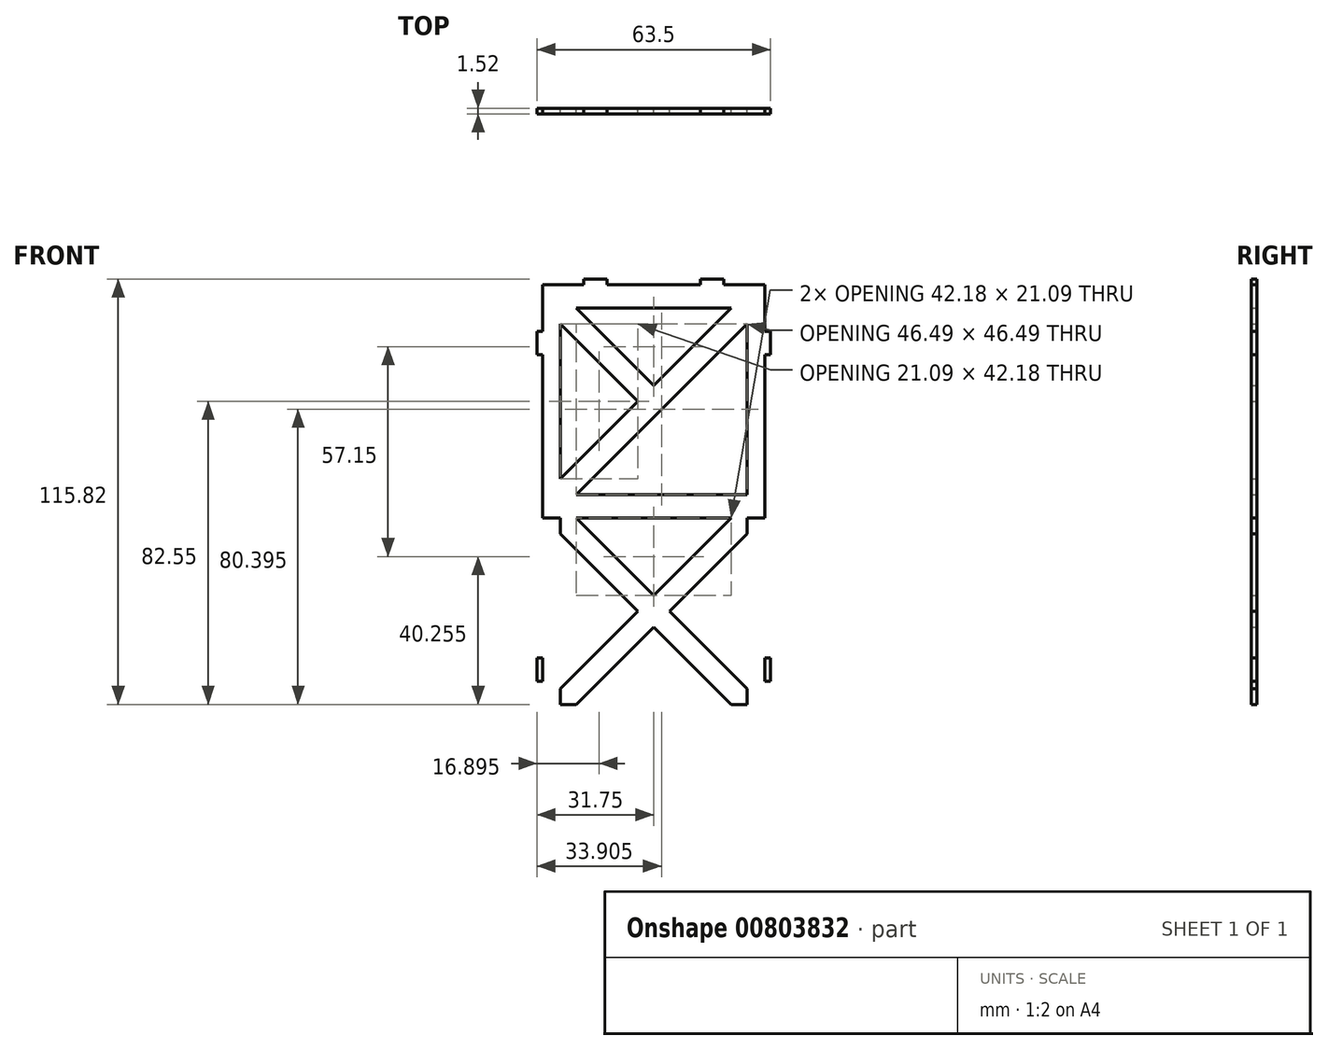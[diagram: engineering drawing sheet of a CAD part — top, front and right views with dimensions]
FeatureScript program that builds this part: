
annotation { "Feature Type Name" : "Feature", "Feature Type Description" : "" }
export const myFeature = defineFeature(function(context is Context, id is Id, definition is map)
    precondition{}
    {
        {
            var Q0;
            Q0=qCreatedBy(makeId("Front.planeOp"),FACE);
            var sketch = newSketch(context, id + "F0", { "sketchPlane" : qUnion([Q0])});
            skLineSegment(sketch, "E0.bottom", {"start": v(31.75, 31.75) * mm, "end": v(-31.75, 31.75) * mm});
            skLineSegment(sketch, "E0.top", {"start": v(31.75, -31.75) * mm, "end": v(-31.75, -31.75) * mm});
            skLineSegment(sketch, "E0.left", {"start": v(31.75, 31.75) * mm, "end": v(31.75, -31.75) * mm});
            skLineSegment(sketch, "E0.right", {"start": v(-31.75, 31.75) * mm, "end": v(-31.75, -31.75) * mm});
            skPoint(sketch, "E0.middle", {"position": v(0, 0) * mm});
            skLineSegment(sketch, "E1.bottom", {"start": v(-19.05, -31.75) * mm, "end": v(-12.7, -31.75) * mm});
            skLineSegment(sketch, "E1.top", {"start": v(-19.05, -33.27) * mm, "end": v(-12.7, -33.27) * mm});
            skLineSegment(sketch, "E1.left", {"start": v(-19.05, -31.75) * mm, "end": v(-19.05, -33.27) * mm});
            skLineSegment(sketch, "E1.right", {"start": v(-12.7, -31.75) * mm, "end": v(-12.7, -33.27) * mm});
            skPoint(sketch, "E2", {"position": v(-15.88, -31.75) * mm});
            skLineSegment(sketch, "E3.MirrorCS", {"start": v(19.05, -31.75) * mm, "end": v(12.7, -31.75) * mm});
            skPoint(sketch, "E4.MirrorP", {"position": v(15.88, -31.75) * mm});
            skLineSegment(sketch, "E5.MirrorCS", {"start": v(19.05, -33.27) * mm, "end": v(12.7, -33.27) * mm});
            skLineSegment(sketch, "E6.MirrorCS", {"start": v(12.7, -31.75) * mm, "end": v(12.7, -33.27) * mm});
            skLineSegment(sketch, "E7.MirrorCS", {"start": v(19.05, -31.75) * mm, "end": v(19.05, -33.27) * mm});
            skLineSegment(sketch, "E8.bottom", {"start": v(-31.75, -19.05) * mm, "end": v(-30.23, -19.05) * mm});
            skLineSegment(sketch, "E8.top", {"start": v(-31.75, -12.7) * mm, "end": v(-30.23, -12.7) * mm});
            skLineSegment(sketch, "E8.left", {"start": v(-31.75, -19.05) * mm, "end": v(-31.75, -12.7) * mm});
            skLineSegment(sketch, "E8.right", {"start": v(-30.23, -19.05) * mm, "end": v(-30.23, -12.7) * mm});
            skPoint(sketch, "E9", {"position": v(-31.75, -15.88) * mm});
            skLineSegment(sketch, "E10.MirrorCS", {"start": v(-31.75, 19.05) * mm, "end": v(-30.23, 19.05) * mm});
            skPoint(sketch, "E11.MirrorP", {"position": v(-31.75, 15.88) * mm});
            skLineSegment(sketch, "E12.MirrorCS", {"start": v(-31.75, 12.7) * mm, "end": v(-30.23, 12.7) * mm});
            skLineSegment(sketch, "E13.MirrorCS", {"start": v(-31.75, 19.05) * mm, "end": v(-31.75, 12.7) * mm});
            skLineSegment(sketch, "E14.MirrorCS", {"start": v(-30.23, 19.05) * mm, "end": v(-30.23, 12.7) * mm});
            skLineSegment(sketch, "E15.MirrorCS", {"start": v(31.75, 19.05) * mm, "end": v(30.23, 19.05) * mm});
            skLineSegment(sketch, "E16.MirrorCS", {"start": v(31.75, -19.05) * mm, "end": v(30.23, -19.05) * mm});
            skLineSegment(sketch, "E17.MirrorCS", {"start": v(31.75, -12.7) * mm, "end": v(30.23, -12.7) * mm});
            skLineSegment(sketch, "E18.MirrorCS", {"start": v(31.75, 12.7) * mm, "end": v(30.23, 12.7) * mm});
            skLineSegment(sketch, "E19.MirrorCS", {"start": v(30.23, 19.05) * mm, "end": v(30.23, 12.7) * mm});
            skLineSegment(sketch, "E20.MirrorCS", {"start": v(30.23, -19.05) * mm, "end": v(30.23, -12.7) * mm});
            skLineSegment(sketch, "E21.MirrorCS", {"start": v(31.75, 19.05) * mm, "end": v(31.75, 12.7) * mm});
            skLineSegment(sketch, "E22.MirrorCS", {"start": v(31.75, -19.05) * mm, "end": v(31.75, -12.7) * mm});
            skPoint(sketch, "E23.MirrorP", {"position": v(31.75, 15.88) * mm});
            skPoint(sketch, "E24.MirrorP", {"position": v(31.75, -15.88) * mm});
            skLineSegment(sketch, "E25.0", {"start": v(-30.23, 31.75) * mm, "end": v(-30.23, -31.75) * mm});
            skLineSegment(sketch, "E26.MirrorCS", {"start": v(30.23, 31.75) * mm, "end": v(30.23, -31.75) * mm});
            skLineSegment(sketch, "E27.bottom", {"start": v(25.4, 25.4) * mm, "end": v(-25.4, 25.4) * mm});
            skLineSegment(sketch, "E27.top", {"start": v(25.4, -25.4) * mm, "end": v(-25.4, -25.4) * mm});
            skLineSegment(sketch, "E27.left", {"start": v(25.4, 25.4) * mm, "end": v(25.4, -25.4) * mm});
            skLineSegment(sketch, "E27.right", {"start": v(-25.4, 25.4) * mm, "end": v(-25.4, -25.4) * mm});
            skLineSegment(sketch, "E28", {"start": v(-25.4, -25.4) * mm, "end": v(25.4, 25.4) * mm, "construction": true});
            skLineSegment(sketch, "E29", {"start": v(-25.4, 25.4) * mm, "end": v(25.4, -25.4) * mm, "construction": true});
            skLineSegment(sketch, "E30.0", {"start": v(-27.56, 23.24) * mm, "end": v(23.24, -27.56) * mm});
            skLineSegment(sketch, "E31.0", {"start": v(-23.24, 27.56) * mm, "end": v(27.56, -23.24) * mm});
            skLineSegment(sketch, "E32.0", {"start": v(-23.24, -27.56) * mm, "end": v(27.56, 23.24) * mm});
            skLineSegment(sketch, "E33.0", {"start": v(-27.56, -23.24) * mm, "end": v(23.24, 27.56) * mm});
            skLineSegment(sketch, "E34.MirrorCS", {"start": v(-12.7, 31.75) * mm, "end": v(-12.7, 33.27) * mm});
            skLineSegment(sketch, "E35.MirrorCS", {"start": v(19.05, 31.75) * mm, "end": v(19.05, 33.27) * mm});
            skLineSegment(sketch, "E36.MirrorCS", {"start": v(12.7, 31.75) * mm, "end": v(12.7, 33.27) * mm});
            skLineSegment(sketch, "E37.MirrorCS", {"start": v(-19.05, 31.75) * mm, "end": v(-19.05, 33.27) * mm});
            skPoint(sketch, "E38.MirrorP", {"position": v(-15.88, 31.75) * mm});
            skLineSegment(sketch, "E39.MirrorCS", {"start": v(19.05, 31.75) * mm, "end": v(12.7, 31.75) * mm});
            skLineSegment(sketch, "E40.MirrorCS", {"start": v(19.05, 33.27) * mm, "end": v(12.7, 33.27) * mm});
            skPoint(sketch, "E41.MirrorP", {"position": v(15.88, 31.75) * mm});
            skLineSegment(sketch, "E42.MirrorCS", {"start": v(-19.05, 33.27) * mm, "end": v(-12.7, 33.27) * mm});
            skLineSegment(sketch, "E43.MirrorCS", {"start": v(-19.05, 31.75) * mm, "end": v(-12.7, 31.75) * mm});
            skLineSegment(sketch, "E44.MirrorCS", {"start": v(19.05, 31.75) * mm, "end": v(19.05, 30.23) * mm});
            skLineSegment(sketch, "E45.MirrorCS", {"start": v(-12.7, 31.75) * mm, "end": v(-12.7, 30.23) * mm});
            skLineSegment(sketch, "E46.MirrorCS", {"start": v(-19.05, 31.75) * mm, "end": v(-19.05, 30.23) * mm});
            skLineSegment(sketch, "E47.MirrorCS", {"start": v(12.7, 31.75) * mm, "end": v(12.7, 30.23) * mm});
            skLineSegment(sketch, "E48.MirrorCS", {"start": v(-19.05, 30.23) * mm, "end": v(-12.7, 30.23) * mm});
            skLineSegment(sketch, "E49.MirrorCS", {"start": v(19.05, 30.23) * mm, "end": v(12.7, 30.23) * mm});
            skLineSegment(sketch, "E50", {"start": v(0, 25.4) * mm, "end": v(0, 31.75) * mm});
            skLineSegment(sketch, "E51", {"start": v(0, 28.58) * mm, "end": v(30.23, 28.58) * mm, "construction": true});
            skLineSegment(sketch, "E52.MirrorCS", {"start": v(-19.05, 25.4) * mm, "end": v(-19.05, 26.92) * mm});
            skLineSegment(sketch, "E53.MirrorCS", {"start": v(19.05, 25.4) * mm, "end": v(19.05, 23.88) * mm});
            skLineSegment(sketch, "E54.MirrorCS", {"start": v(-12.7, 25.4) * mm, "end": v(-12.7, 26.92) * mm});
            skLineSegment(sketch, "E55.MirrorCS", {"start": v(19.05, 25.4) * mm, "end": v(19.05, 26.92) * mm});
            skLineSegment(sketch, "E56.MirrorCS", {"start": v(12.7, 25.4) * mm, "end": v(12.7, 26.92) * mm});
            skLineSegment(sketch, "E57.MirrorCS", {"start": v(-19.05, 25.4) * mm, "end": v(-19.05, 23.88) * mm});
            skLineSegment(sketch, "E58.MirrorCS", {"start": v(12.7, 25.4) * mm, "end": v(12.7, 23.88) * mm});
            skLineSegment(sketch, "E59.MirrorCS", {"start": v(-12.7, 25.4) * mm, "end": v(-12.7, 23.88) * mm});
            skLineSegment(sketch, "E60.MirrorCS", {"start": v(19.05, 25.4) * mm, "end": v(12.7, 25.4) * mm});
            skLineSegment(sketch, "E61.MirrorCS", {"start": v(-19.05, 25.4) * mm, "end": v(-12.7, 25.4) * mm});
            skLineSegment(sketch, "E62.MirrorCS", {"start": v(-31.75, 76.2) * mm, "end": v(-30.23, 76.2) * mm});
            skLineSegment(sketch, "E63.MirrorCS", {"start": v(-19.05, 23.88) * mm, "end": v(-12.7, 23.88) * mm});
            skLineSegment(sketch, "E64.MirrorCS", {"start": v(-31.75, 38.1) * mm, "end": v(-30.23, 38.1) * mm});
            skLineSegment(sketch, "E65.MirrorCS", {"start": v(-19.05, 26.92) * mm, "end": v(-12.7, 26.92) * mm});
            skLineSegment(sketch, "E66.MirrorCS", {"start": v(31.75, 44.45) * mm, "end": v(30.23, 44.45) * mm});
            skLineSegment(sketch, "E67.MirrorCS", {"start": v(31.75, 76.2) * mm, "end": v(30.23, 76.2) * mm});
            skLineSegment(sketch, "E68.MirrorCS", {"start": v(19.05, 26.92) * mm, "end": v(12.7, 26.92) * mm});
            skLineSegment(sketch, "E69.MirrorCS", {"start": v(31.75, 69.85) * mm, "end": v(30.23, 69.85) * mm});
            skLineSegment(sketch, "E70.MirrorCS", {"start": v(-31.75, 69.85) * mm, "end": v(-30.23, 69.85) * mm});
            skLineSegment(sketch, "E71.MirrorCS", {"start": v(19.05, 23.88) * mm, "end": v(12.7, 23.88) * mm});
            skLineSegment(sketch, "E72.MirrorCS", {"start": v(-31.75, 44.45) * mm, "end": v(-30.23, 44.45) * mm});
            skLineSegment(sketch, "E73.MirrorCS", {"start": v(19.05, 88.9) * mm, "end": v(19.05, 90.42) * mm});
            skPoint(sketch, "E74.MirrorP", {"position": v(0, 57.15) * mm});
            skLineSegment(sketch, "E75.MirrorCS", {"start": v(12.7, 88.9) * mm, "end": v(12.7, 90.42) * mm});
            skLineSegment(sketch, "E76.MirrorCS", {"start": v(-12.7, 88.9) * mm, "end": v(-12.7, 90.42) * mm});
            skLineSegment(sketch, "E77.MirrorCS", {"start": v(31.75, 38.1) * mm, "end": v(30.23, 38.1) * mm});
            skLineSegment(sketch, "E78.MirrorCS", {"start": v(-19.05, 88.9) * mm, "end": v(-19.05, 90.42) * mm});
            skLineSegment(sketch, "E79.MirrorCS", {"start": v(-31.75, 38.1) * mm, "end": v(-31.75, 44.45) * mm});
            skLineSegment(sketch, "E80.MirrorCS", {"start": v(30.23, 76.2) * mm, "end": v(30.23, 69.85) * mm});
            skPoint(sketch, "E81.MirrorP", {"position": v(-15.88, 25.4) * mm});
            skLineSegment(sketch, "E82.MirrorCS", {"start": v(-31.75, 76.2) * mm, "end": v(-31.75, 69.85) * mm});
            skLineSegment(sketch, "E83.MirrorCS", {"start": v(-30.23, 76.2) * mm, "end": v(-30.23, 69.85) * mm});
            skLineSegment(sketch, "E84.MirrorCS", {"start": v(0, 31.75) * mm, "end": v(0, 25.4) * mm});
            skLineSegment(sketch, "E85.MirrorCS", {"start": v(-19.05, 88.9) * mm, "end": v(-12.7, 88.9) * mm});
            skLineSegment(sketch, "E86.MirrorCS", {"start": v(19.05, 88.9) * mm, "end": v(12.7, 88.9) * mm});
            skLineSegment(sketch, "E87.MirrorCS", {"start": v(-30.23, 38.1) * mm, "end": v(-30.23, 44.45) * mm});
            skLineSegment(sketch, "E88.MirrorCS", {"start": v(19.05, 90.42) * mm, "end": v(12.7, 90.42) * mm});
            skLineSegment(sketch, "E89.MirrorCS", {"start": v(31.75, 38.1) * mm, "end": v(31.75, 44.45) * mm});
            skPoint(sketch, "E90.MirrorP", {"position": v(15.88, 25.4) * mm});
            skLineSegment(sketch, "E91.MirrorCS", {"start": v(31.75, 76.2) * mm, "end": v(31.75, 69.85) * mm});
            skLineSegment(sketch, "E92.MirrorCS", {"start": v(-19.05, 90.42) * mm, "end": v(-12.7, 90.42) * mm});
            skLineSegment(sketch, "E93.MirrorCS", {"start": v(30.23, 38.1) * mm, "end": v(30.23, 44.45) * mm});
            skLineSegment(sketch, "E94.MirrorCS", {"start": v(-27.56, 80.4) * mm, "end": v(23.24, 29.6) * mm});
            skLineSegment(sketch, "E95.MirrorCS", {"start": v(-30.23, 25.4) * mm, "end": v(-30.23, 88.9) * mm});
            skLineSegment(sketch, "E96.MirrorCS", {"start": v(25.4, 31.75) * mm, "end": v(-25.4, 31.75) * mm});
            skLineSegment(sketch, "E97.MirrorCS", {"start": v(-23.24, 29.6) * mm, "end": v(27.56, 80.4) * mm});
            skPoint(sketch, "E98.MirrorP", {"position": v(-15.88, 88.9) * mm});
            skPoint(sketch, "E99.MirrorP", {"position": v(15.88, 88.9) * mm});
            skLineSegment(sketch, "E100.MirrorCS", {"start": v(-27.56, 33.9) * mm, "end": v(23.24, 84.7) * mm});
            skLineSegment(sketch, "E101.MirrorCS", {"start": v(30.23, 25.4) * mm, "end": v(30.23, 88.9) * mm});
            skLineSegment(sketch, "E102.MirrorCS", {"start": v(25.4, 82.55) * mm, "end": v(-25.4, 82.55) * mm});
            skLineSegment(sketch, "E103.MirrorCS", {"start": v(-23.24, 84.7) * mm, "end": v(27.56, 33.9) * mm});
            skPoint(sketch, "E104.MirrorP", {"position": v(-31.75, 41.28) * mm});
            skLineSegment(sketch, "E105.MirrorCS", {"start": v(31.75, 25.4) * mm, "end": v(-31.75, 25.4) * mm});
            skLineSegment(sketch, "E106.MirrorCS", {"start": v(-25.4, 31.75) * mm, "end": v(-25.4, 82.55) * mm});
            skLineSegment(sketch, "E107.MirrorCS", {"start": v(31.75, 88.9) * mm, "end": v(-31.75, 88.9) * mm});
            skLineSegment(sketch, "E108.MirrorCS", {"start": v(31.75, 25.4) * mm, "end": v(31.75, 88.9) * mm});
            skLineSegment(sketch, "E109.MirrorCS", {"start": v(-31.75, 25.4) * mm, "end": v(-31.75, 88.9) * mm});
            skPoint(sketch, "E110.MirrorP", {"position": v(-31.75, 73.03) * mm});
            skPoint(sketch, "E111.MirrorP", {"position": v(31.75, 73.03) * mm});
            skLineSegment(sketch, "E112.MirrorCS", {"start": v(25.4, 31.75) * mm, "end": v(25.4, 82.55) * mm});
            skLineSegment(sketch, "E113.MirrorCS", {"start": v(-25.4, 31.75) * mm, "end": v(25.4, 82.55) * mm, "construction": true});
            skPoint(sketch, "E114.MirrorP", {"position": v(31.75, 41.28) * mm});
            skLineSegment(sketch, "E115.MirrorCS", {"start": v(-25.4, 82.55) * mm, "end": v(25.4, 31.75) * mm, "construction": true});
            skSolve(sketch);
        }
        {
            var Q0;
            {var subQ21=sQuery(id+"F0.wireOp",EDGE,"E1.bottom");Q0=makeQuery(id+"F0.imprint","IMPRINT",FACE,{"disambiguationData":[TD([[makeQuery(id+"F0.imprint","IMPRINT",EDGE,{"derivedFrom":subQ21}),1.0]])]});}
            var Q1;
            {var subQ0=sQuery(id+"F0.wireOp",EDGE,"E8.bottom");Q1=makeQuery(id+"F0.imprint","IMPRINT",FACE,{"disambiguationData":[TD([[makeQuery(id+"F0.imprint","IMPRINT",EDGE,{"derivedFrom":subQ0}),1.0]])]});}
            var Q2;
            Q2=makeQuery(id+"F0.imprint","IMPRINT",FACE,{"disambiguationData":[TD([[makeQuery(id+"F0.imprint","IMPRINT",EDGE,{"derivedFrom":sQuery(id+"F0.wireOp",EDGE,"E1.bottom")}),-1.0]])]});
            var Q3;
            Q3=makeQuery(id+"F0.imprint","IMPRINT",FACE,{"disambiguationData":[TD([[makeQuery(id+"F0.imprint","IMPRINT",EDGE,{"derivedFrom":sQuery(id+"F0.wireOp",EDGE,"E3.MirrorCS")}),1.0]])]});
            var Q4;
            {var subQ1=sQuery(id+"F0.wireOp",EDGE,"E27.left");var subQ6=sQuery(id+"F0.wireOp",EDGE,"E27.top");var subQ9=makeQuery(id+"F0.imprint","INTERSECT",VERTEX,{"derivedFrom":[subQ6,subQ1]});Q4=makeQuery(id+"F0.imprint","IMPRINT",FACE,{"disambiguationData":[TD([[makeQuery(id+"F0.imprint","IMPRINT",EDGE,{"disambiguationData":[TD([[subQ9,-1.0]])],"derivedFrom":subQ6}),-1.0]])]});}
            var Q5;
            {var subQ0=sQuery(id+"F0.wireOp",EDGE,"E33.0");var subQ1=sQuery(id+"F0.wireOp",EDGE,"E30.0");var subQ2=makeQuery(id+"F0.imprint","INTERSECT",VERTEX,{"derivedFrom":[subQ1,subQ0]});Q5=makeQuery(id+"F0.imprint","IMPRINT",FACE,{"disambiguationData":[TD([[makeQuery(id+"F0.imprint","IMPRINT",EDGE,{"disambiguationData":[TD([[subQ2,-1.0]])],"derivedFrom":subQ1}),1.0]])]});}
            var Q6;
            {var subQ0=sQuery(id+"F0.wireOp",EDGE,"E105.MirrorCS");var subQ5=sQuery(id+"F0.wireOp",EDGE,"E27.left");var subQ6=makeQuery(id+"F0.imprint","INTERSECT",VERTEX,{"derivedFrom":[subQ5,subQ0]});Q6=makeQuery(id+"F0.imprint","IMPRINT",FACE,{"disambiguationData":[TD([[makeQuery(id+"F0.imprint","IMPRINT",EDGE,{"disambiguationData":[TD([[subQ6,-1.0]])],"derivedFrom":subQ5}),-1.0]])]});}
            var Q7;
            {var subQ0=sQuery(id+"F0.wireOp",EDGE,"E105.MirrorCS");var subQ7=sQuery(id+"F0.wireOp",EDGE,"E27.right");var subQ9=makeQuery(id+"F0.imprint","INTERSECT",VERTEX,{"derivedFrom":[subQ7,subQ0]});Q7=makeQuery(id+"F0.imprint","IMPRINT",FACE,{"disambiguationData":[TD([[makeQuery(id+"F0.imprint","IMPRINT",EDGE,{"disambiguationData":[TD([[subQ9,-1.0]])],"derivedFrom":subQ7}),1.0]])]});}
            var Q8;
            {var subQ1=sQuery(id+"F0.wireOp",EDGE,"E27.top");var subQ7=sQuery(id+"F0.wireOp",EDGE,"E27.right");var subQ8=makeQuery(id+"F0.imprint","INTERSECT",VERTEX,{"derivedFrom":[subQ1,subQ7]});Q8=makeQuery(id+"F0.imprint","IMPRINT",FACE,{"disambiguationData":[TD([[makeQuery(id+"F0.imprint","IMPRINT",EDGE,{"disambiguationData":[TD([[subQ8,1.0]])],"derivedFrom":subQ1}),-1.0]])]});}
            var Q9;
            {var subQ12=sQuery(id+"F0.wireOp",EDGE,"E45.MirrorCS");Q9=makeQuery(id+"F0.imprint","IMPRINT",FACE,{"disambiguationData":[TD([[makeQuery(id+"F0.imprint","IMPRINT",EDGE,{"derivedFrom":subQ12}),1.0]])]});}
            var Q10;
            {var subQ0=sQuery(id+"F0.wireOp",EDGE,"E52.MirrorCS");Q10=makeQuery(id+"F0.imprint","IMPRINT",FACE,{"disambiguationData":[TD([[makeQuery(id+"F0.imprint","IMPRINT",EDGE,{"derivedFrom":subQ0}),-1.0]])]});}
            var Q11;
            {var subQ2=sQuery(id+"F0.wireOp",EDGE,"E44.MirrorCS");Q11=makeQuery(id+"F0.imprint","IMPRINT",FACE,{"disambiguationData":[TD([[makeQuery(id+"F0.imprint","IMPRINT",EDGE,{"derivedFrom":subQ2}),1.0]])]});}
            var Q12;
            {var subQ0=sQuery(id+"F0.wireOp",EDGE,"E55.MirrorCS");Q12=makeQuery(id+"F0.imprint","IMPRINT",FACE,{"disambiguationData":[TD([[makeQuery(id+"F0.imprint","IMPRINT",EDGE,{"derivedFrom":subQ0}),1.0]])]});}
            var Q13;
            {var subQ0=sQuery(id+"F0.wireOp",EDGE,"E44.MirrorCS");Q13=makeQuery(id+"F0.imprint","IMPRINT",FACE,{"disambiguationData":[TD([[makeQuery(id+"F0.imprint","IMPRINT",EDGE,{"derivedFrom":subQ0}),-1.0]])]});}
            var Q14;
            {var subQ4=sQuery(id+"F0.wireOp",EDGE,"E95.MirrorCS");var subQ5=makeQuery(id+"F0.imprint","INTERSECT",VERTEX,{"derivedFrom":[sQuery(id+"F0.wireOp",EDGE,"E64.MirrorCS"),subQ4]});Q14=makeQuery(id+"F0.imprint","IMPRINT",FACE,{"disambiguationData":[TD([[makeQuery(id+"F0.imprint","IMPRINT",EDGE,{"disambiguationData":[TD([[subQ5,1.0]])],"derivedFrom":subQ4}),-1.0]])]});}
            var Q15;
            {var subQ1=sQuery(id+"F0.wireOp",EDGE,"E100.MirrorCS");var subQ3=sQuery(id+"F0.wireOp",EDGE,"E94.MirrorCS");var subQ4=makeQuery(id+"F0.imprint","INTERSECT",VERTEX,{"derivedFrom":[subQ3,subQ1]});Q15=makeQuery(id+"F0.imprint","IMPRINT",FACE,{"disambiguationData":[TD([[makeQuery(id+"F0.imprint","IMPRINT",EDGE,{"disambiguationData":[TD([[subQ4,-1.0]])],"derivedFrom":subQ3}),-1.0]])]});}
            var Q16;
            {var subQ0=sQuery(id+"F0.wireOp",EDGE,"E100.MirrorCS");var subQ1=sQuery(id+"F0.wireOp",EDGE,"E94.MirrorCS");var subQ2=makeQuery(id+"F0.imprint","INTERSECT",VERTEX,{"derivedFrom":[subQ1,subQ0]});Q16=makeQuery(id+"F0.imprint","IMPRINT",FACE,{"disambiguationData":[TD([[makeQuery(id+"F0.imprint","IMPRINT",EDGE,{"disambiguationData":[TD([[subQ2,-1.0]])],"derivedFrom":subQ1}),1.0]])]});}
            var Q17;
            {var subQ1=sQuery(id+"F0.wireOp",EDGE,"E97.MirrorCS");var subQ7=sQuery(id+"F0.wireOp",EDGE,"E112.MirrorCS");var subQ9=makeQuery(id+"F0.imprint","INTERSECT",VERTEX,{"derivedFrom":[subQ1,subQ7]});Q17=makeQuery(id+"F0.imprint","IMPRINT",FACE,{"disambiguationData":[TD([[makeQuery(id+"F0.imprint","IMPRINT",EDGE,{"disambiguationData":[TD([[subQ9,1.0]])],"derivedFrom":subQ1}),1.0]])]});}
            var Q18;
            {var subQ1=sQuery(id+"F0.wireOp",EDGE,"E94.MirrorCS");var subQ7=sQuery(id+"F0.wireOp",EDGE,"E96.MirrorCS");var subQ9=makeQuery(id+"F0.imprint","INTERSECT",VERTEX,{"derivedFrom":[subQ1,subQ7]});Q18=makeQuery(id+"F0.imprint","IMPRINT",FACE,{"disambiguationData":[TD([[makeQuery(id+"F0.imprint","IMPRINT",EDGE,{"disambiguationData":[TD([[subQ9,1.0]])],"derivedFrom":subQ1}),1.0]])]});}
            var Q19;
            {var subQ5=sQuery(id+"F0.wireOp",EDGE,"E94.MirrorCS");var subQ7=sQuery(id+"F0.wireOp",EDGE,"E106.MirrorCS");var subQ9=makeQuery(id+"F0.imprint","INTERSECT",VERTEX,{"derivedFrom":[subQ5,subQ7]});Q19=makeQuery(id+"F0.imprint","IMPRINT",FACE,{"disambiguationData":[TD([[makeQuery(id+"F0.imprint","IMPRINT",EDGE,{"disambiguationData":[TD([[subQ9,-1.0]])],"derivedFrom":subQ5}),1.0]])]});}
            var Q20;
            {var subQ0=sQuery(id+"F0.wireOp",EDGE,"E73.MirrorCS");Q20=makeQuery(id+"F0.imprint","IMPRINT",FACE,{"disambiguationData":[TD([[makeQuery(id+"F0.imprint","IMPRINT",EDGE,{"derivedFrom":subQ0}),1.0]])]});}
            var Q21;
            {var subQ0=sQuery(id+"F0.wireOp",EDGE,"E76.MirrorCS");Q21=makeQuery(id+"F0.imprint","IMPRINT",FACE,{"disambiguationData":[TD([[makeQuery(id+"F0.imprint","IMPRINT",EDGE,{"derivedFrom":subQ0}),1.0]])]});}
            var Q22;
            {var subQ0=sQuery(id+"F0.wireOp",EDGE,"E62.MirrorCS");Q22=makeQuery(id+"F0.imprint","IMPRINT",FACE,{"disambiguationData":[TD([[makeQuery(id+"F0.imprint","IMPRINT",EDGE,{"derivedFrom":subQ0}),-1.0]])]});}
            var Q23;
            {var subQ0=sQuery(id+"F0.wireOp",EDGE,"E67.MirrorCS");Q23=makeQuery(id+"F0.imprint","IMPRINT",FACE,{"disambiguationData":[TD([[makeQuery(id+"F0.imprint","IMPRINT",EDGE,{"derivedFrom":subQ0}),1.0]])]});}
            var Q24;
            {var subQ0=sQuery(id+"F0.wireOp",EDGE,"E16.MirrorCS");Q24=makeQuery(id+"F0.imprint","IMPRINT",FACE,{"disambiguationData":[TD([[makeQuery(id+"F0.imprint","IMPRINT",EDGE,{"derivedFrom":subQ0}),-1.0]])]});}
            var Q25;
            {var subQ0=sQuery(id+"F0.wireOp",EDGE,"E45.MirrorCS");Q25=makeQuery(id+"F0.imprint","IMPRINT",FACE,{"disambiguationData":[TD([[makeQuery(id+"F0.imprint","IMPRINT",EDGE,{"derivedFrom":subQ0}),-1.0]])]});}
            extrude(context, id + "F1", {"entities" : qUnion([Q0, Q1, Q2, Q3, Q4, Q5, Q6, Q7, Q8, Q9, Q10, Q11, Q12, Q13, Q14, Q15, Q16, Q17, Q18, Q19, Q20, Q21, Q22, Q23, Q24, Q25]), "depth" : 1.52 * mm, "offsetDistance" : 25.4 * mm});
        }
    });
